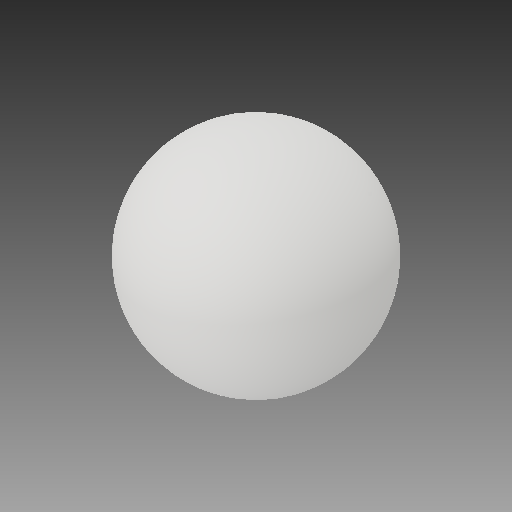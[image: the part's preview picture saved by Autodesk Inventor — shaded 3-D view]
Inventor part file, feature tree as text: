
AUTODESK INVENTOR PART (.ipt)
format: ipt  version: 2017 (Build 210142000, 142)  size: 119,296 bytes
history: native  units: in
note: dims shown in document units (in); Inventor stores cm internally (conversion verified against a paired STEP export)
features: revolve x1
ambient origin geometry x8: Origin, YZ Plane, XZ Plane, XY Plane, X Axis, Y Axis, Z Axis, Center Point
bodies: Solid1 (feature_tree)
feature tree (1):
  revolve  "Revolve1"  [1 undecoded]
note: 1 required parameter value undecoded (feature->parameter linkage not recoverable at this tier; creation-order binding heuristic only, values carry confidence <= 0.55)
